FCSTD DOCUMENT  (FreeCAD 0.21R32532 (Git))
Label: hollow-pad
License: All rights reserved
LicenseURL: http://en.wikipedia.org/wiki/All_rights_reserved
objects: Sketcher::SketchObject×3, App::Annotation×2, App::DocumentObjectGroup×1
note: 3 computed .brp shape members not serialized (recipe doc carries the construction recipe); baked Part::Feature solids carry a one-line shape summary decoded from their .brp

FEATURE [Sketcher::SketchObject] Sketch  label="Pads_Poly_Arc1_padNum=1"
  FullyConstrained = true
  sketch-geometry (5):
    g0: ArcOfCircle CenterX=0 CenterY=0 CenterZ=0 NormalX=0 NormalY=0 NormalZ=1 AngleXU=0 Radius=10 StartAngle=4.71239 EndAngle=7.85398
    g1: ArcOfCircle CenterX=0 CenterY=0 CenterZ=0 NormalX=0 NormalY=0 NormalZ=1 AngleXU=0 Radius=3.5 StartAngle=4.71239 EndAngle=7.85398
    g2: LineSegment StartX=1.35503e-05 StartY=10 StartZ=0 EndX=1.35503e-05 EndY=3.5 EndZ=0
    g3: LineSegment StartX=-1.35504e-05 StartY=-3.5 StartZ=0 EndX=-1.35504e-05 EndY=-10 EndZ=0
    g4: Circle CenterX=6 CenterY=0 CenterZ=0 NormalX=0 NormalY=0 NormalZ=1 AngleXU=0 Radius=0.75
  constraints (15):
    c: Coincident(g0,g-1)
    c: Radius(g0) = 10
    c: Coincident(g1,g0)
    c: Radius(g1) = 3.5
    c: Coincident(g1,g2)
    c: Coincident(g1,g3)
    c: Coincident(g0,g2)
    c: Coincident(g0,g3)
    c: PointOnObject(g4,g-1)
    c: Radius(g4) = 0.75
    c: DistanceX(g0,g4) = 6
    c: Vertical(g2)
    c: Vertical(g3)
    c: Equal(g2,g3)
    c: DistanceY(g2,g2) = 6.5
FEATURE [Sketcher::SketchObject] Sketch001  label="Pads_Poly_Arc2_padNum=1"
  FullyConstrained = true
  sketch-geometry (7):
    g0: ArcOfCircle CenterX=0 CenterY=0 CenterZ=0 NormalX=0 NormalY=0 NormalZ=1 AngleXU=0 Radius=10 StartAngle=3.78509 EndAngle=4.71239
    g1: LineSegment StartX=-8 StartY=6 StartZ=0 EndX=-8 EndY=-6 EndZ=0
    g2: ArcOfCircle CenterX=0 CenterY=0 CenterZ=0 NormalX=0 NormalY=0 NormalZ=1 AngleXU=0 Radius=3.5 StartAngle=1.5708 EndAngle=4.71239
    g3: LineSegment StartX=4.92945e-11 StartY=10 StartZ=0 EndX=4.92945e-11 EndY=3.5 EndZ=0
    g4: LineSegment StartX=-1.11352e-05 StartY=-3.5 StartZ=0 EndX=-1.11352e-05 EndY=-10 EndZ=0
    g5: ArcOfCircle CenterX=0 CenterY=0 CenterZ=0 NormalX=0 NormalY=0 NormalZ=1 AngleXU=0 Radius=10 StartAngle=1.5708 EndAngle=2.49809
    g6: Circle CenterX=-6 CenterY=0 CenterZ=0 NormalX=0 NormalY=0 NormalZ=1 AngleXU=0 Radius=0.75
  constraints (21):
    c: Coincident(g0,g-1)
    c: Radius(g0) = 10
    c: Vertical(g1)
    c: DistanceY(g0,g1) = 6
    c: Coincident(g5,g1)
    c: Coincident(g0,g1)
    c: Coincident(g2,g0)
    c: Radius(g2) = 3.5
    c: Coincident(g2,g4)
    c: Coincident(g2,g3)
    c: Equal(g0,g5)
    c: Coincident(g0,g4)
    c: Coincident(g5,g3)
    c: Coincident(g0,g5)
    c: PointOnObject(g6,g-1)
    c: Radius(g6) = 0.75
    c: DistanceX(g6,g0) = 6
    c: Equal(g3,g4)
    c: DistanceY(g3,g3) = 6.5
    c: Vertical(g3)
    c: Vertical(g4)
FEATURE [App::Annotation] Text  label="Ref#_1.0mm"
  LabelText = REF**
  Position = (0,4,0)
FEATURE [App::Annotation] Text001  label="Value#_1.0mm"
  LabelText = Value 
  Position = (0,-6,0)
FEATURE [Sketcher::SketchObject] Sketch002  label="Pads_NPTH"
  FullyConstrained = true
  sketch-geometry (1):
    g0: Circle CenterX=0 CenterY=0 CenterZ=0 NormalX=0 NormalY=0 NormalZ=1 AngleXU=0 Radius=2.75
  constraints (2):
    c: Radius(g0) = 2.75
    c: Coincident(g0,g-1)
FEATURE [App::DocumentObjectGroup] Group  label="hollow-pad-fp"
  Group = -> [Text,Text001,Sketch,Sketch001,Sketch002]
